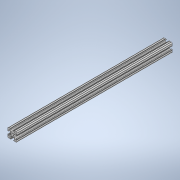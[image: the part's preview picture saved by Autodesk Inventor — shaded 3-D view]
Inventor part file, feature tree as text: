
AUTODESK INVENTOR PART (.ipt)
format: ipt  version: 2020 (Build 240168000, 168)  size: 235,520 bytes
history: native  units: in
note: dims shown in document units (in); Inventor stores cm internally (conversion verified against a paired STEP export)
features: extrude x1, sketch x1
ambient origin geometry x8: Origin, YZ Plane, XZ Plane, XY Plane, X Axis, Y Axis, Z Axis, Center Point
bodies: Solid1 (feature_tree)
feature tree (2):
  extrude  "Extrusion1"  [1 undecoded]
  sketch  "Sketch1"  dims[d0=17.0in d1=0.0in]
note: 1 required parameter value undecoded (feature->parameter linkage not recoverable at this tier; creation-order binding heuristic only, values carry confidence <= 0.55)
